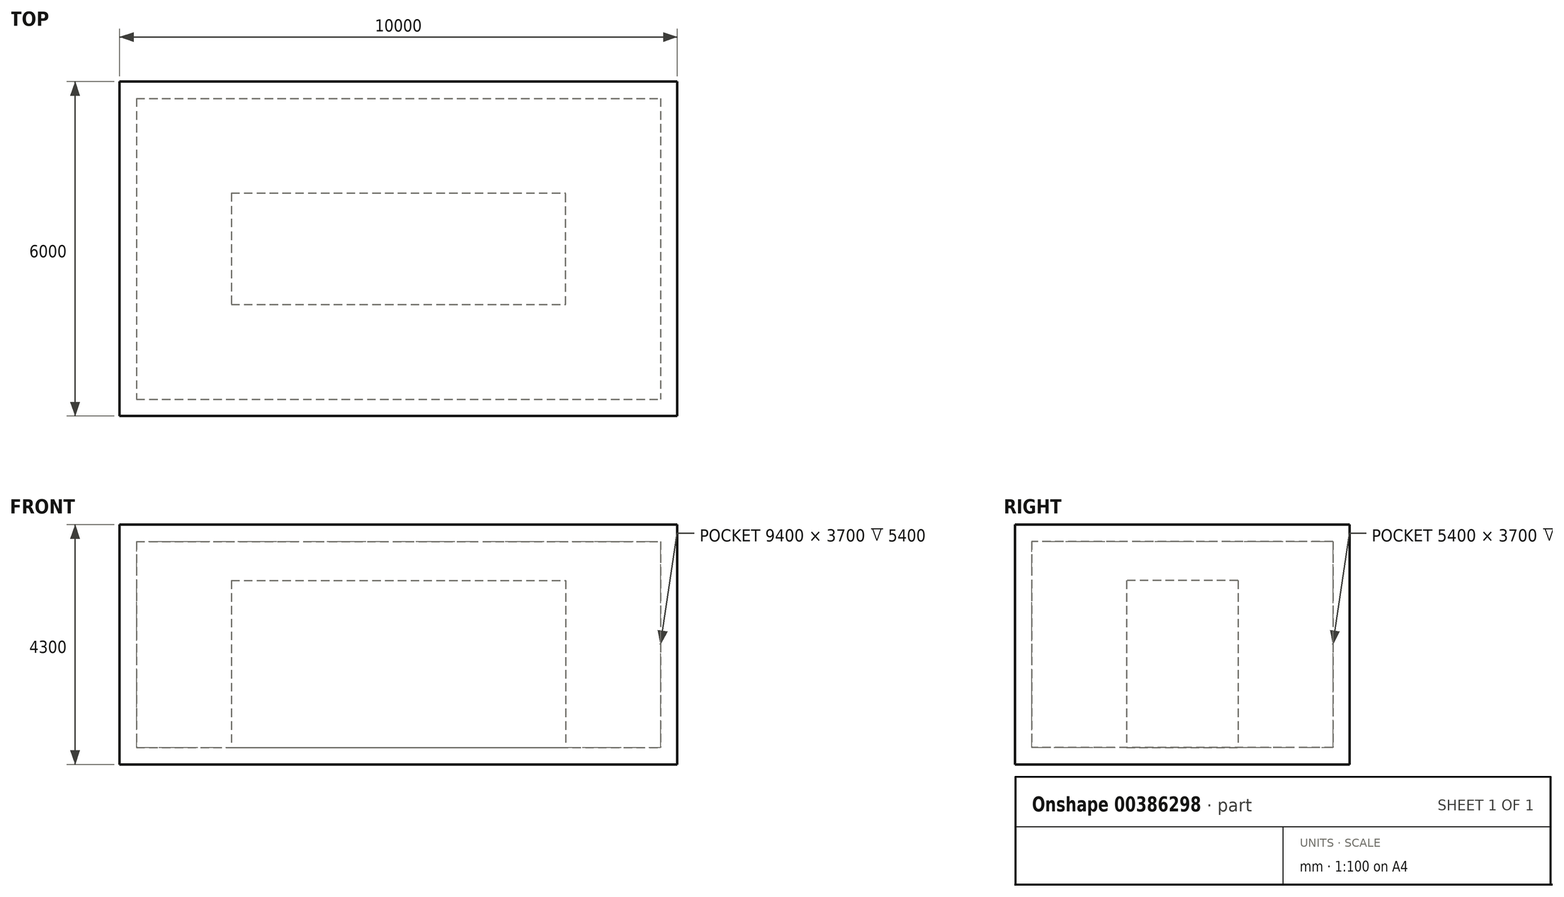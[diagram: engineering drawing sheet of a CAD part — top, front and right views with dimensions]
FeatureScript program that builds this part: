
annotation { "Feature Type Name" : "Feature", "Feature Type Description" : "" }
export const myFeature = defineFeature(function(context is Context, id is Id, definition is map)
    precondition{}
    {
        {
            var Q0;
            Q0=qCreatedBy(makeId("Top.planeOp"),FACE);
            var sketch = newSketch(context, id + "F0", { "sketchPlane" : qUnion([Q0])});
            skLineSegment(sketch, "E0.bottom", {"start": v(-5147.94, 2999.1) * mm, "end": v(4852.06, 2999.1) * mm});
            skLineSegment(sketch, "E0.top", {"start": v(-5147.94, -3000.9) * mm, "end": v(4852.06, -3000.9) * mm});
            skLineSegment(sketch, "E0.left", {"start": v(-5147.94, 2999.1) * mm, "end": v(-5147.94, -3000.9) * mm});
            skLineSegment(sketch, "E0.right", {"start": v(4852.06, 2999.1) * mm, "end": v(4852.06, -3000.9) * mm});
            skSolve(sketch);
        }
        {
            var Q0;
            Q0 = qSketchRegion(id + "F0", true);
            extrude(context, id + "F1", {"entities" : qUnion([Q0]), "depth" : 4000 * mm});
        }
        {
            var Q0;
            Q0=makeQuery(id+"F1.opExtrude","CAP_FACE",FACE,{"disambiguationData":[OSD([sQuery(id+"F0.wireOp",EDGE,"E0.bottom"),sQuery(id+"F0.wireOp",EDGE,"E0.top"),sQuery(id+"F0.wireOp",EDGE,"E0.left"),sQuery(id+"F0.wireOp",EDGE,"E0.right")])],"isStart":false});
            shell(context, id + "F2", {"entities" : qUnion([Q0]), "thickness" : 300 * mm});
        }
        {
            var Q0;
            Q0=makeQuery(id+"F2.opShell","OFFSET_FACE",FACE,{"disambiguationData":[OSD([sQuery(id+"F0.wireOp",EDGE,"E0.bottom"),sQuery(id+"F0.wireOp",EDGE,"E0.top"),sQuery(id+"F0.wireOp",EDGE,"E0.left"),sQuery(id+"F0.wireOp",EDGE,"E0.right")])]});
            var sketch = newSketch(context, id + "F3", { "sketchPlane" : qUnion([Q0])});
            skLineSegment(sketch, "E1.bottom", {"start": v(-3147.94, 999.1) * mm, "end": v(2852.06, 999.1) * mm});
            skLineSegment(sketch, "E1.left", {"start": v(-3147.94, 999.1) * mm, "end": v(-3147.94, -1000.9) * mm});
            skLineSegment(sketch, "E2", {"start": v(-3147.94, -1000.9) * mm, "end": v(2852.06, -1000.9) * mm});
            skLineSegment(sketch, "E3", {"start": v(2852.06, -1000.9) * mm, "end": v(2852.06, 999.1) * mm});
            skSolve(sketch);
        }
        {
            var Q0;
            Q0=makeQuery(id+"F3.imprint","IMPRINT",FACE,{"disambiguationData":[TD([[makeQuery(id+"F3.imprint","IMPRINT",EDGE,{"derivedFrom":sQuery(id+"F3.wireOp",EDGE,"E1.bottom")}),-1.0]])]});
            extrude(context, id + "F4", {"entities" : qUnion([Q0]), "operationType" : NewBodyOperationType.ADD, "depth" : 3000 * mm});
        }
        {
            var Q0;
            Q0=makeQuery(id+"F1.opExtrude","CAP_FACE",FACE,{"disambiguationData":[OSD([sQuery(id+"F0.wireOp",EDGE,"E0.bottom"),sQuery(id+"F0.wireOp",EDGE,"E0.top"),sQuery(id+"F0.wireOp",EDGE,"E0.left"),sQuery(id+"F0.wireOp",EDGE,"E0.right")])],"isStart":false});
            var sketch = newSketch(context, id + "F5", { "sketchPlane" : qUnion([Q0])});
            skSolve(sketch);
        }
        {
            var Q0;
            {var subQ0=sQuery(id+"F0.wireOp",EDGE,"E0.bottom");Q0=makeQuery(id+"F5.imprint","IMPRINT",FACE,{"disambiguationData":[TD([[makeQuery(id+"F5.imprint","IMPRINT",EDGE,{"derivedFrom":makeQuery(id+"F2.opShell","OFFSET_EDGE",EDGE,{"disambiguationData":[OSD([subQ0]),TDD([makeQuery(id+"F1.opExtrude","CAP_EDGE",EDGE,{"disambiguationData":[OSD([subQ0])],"isStart":false})])]})}),-1.0]])]});}
            var Q1;
            {var subQ6=sQuery(id+"F0.wireOp",EDGE,"E0.bottom");var subQ7=makeQuery(id+"F1.opExtrude","CAP_EDGE",EDGE,{"disambiguationData":[OSD([subQ6])],"isStart":false});Q1=makeQuery(id+"F5.imprint","IMPRINT",FACE,{"disambiguationData":[TD([[makeQuery(id+"F5.imprint","IMPRINT",EDGE,{"derivedFrom":subQ7}),-1.0]])]});}
            extrude(context, id + "F6", {"entities" : qUnion([Q0, Q1]), "operationType" : NewBodyOperationType.ADD, "depth" : 300 * mm});
        }
    });
